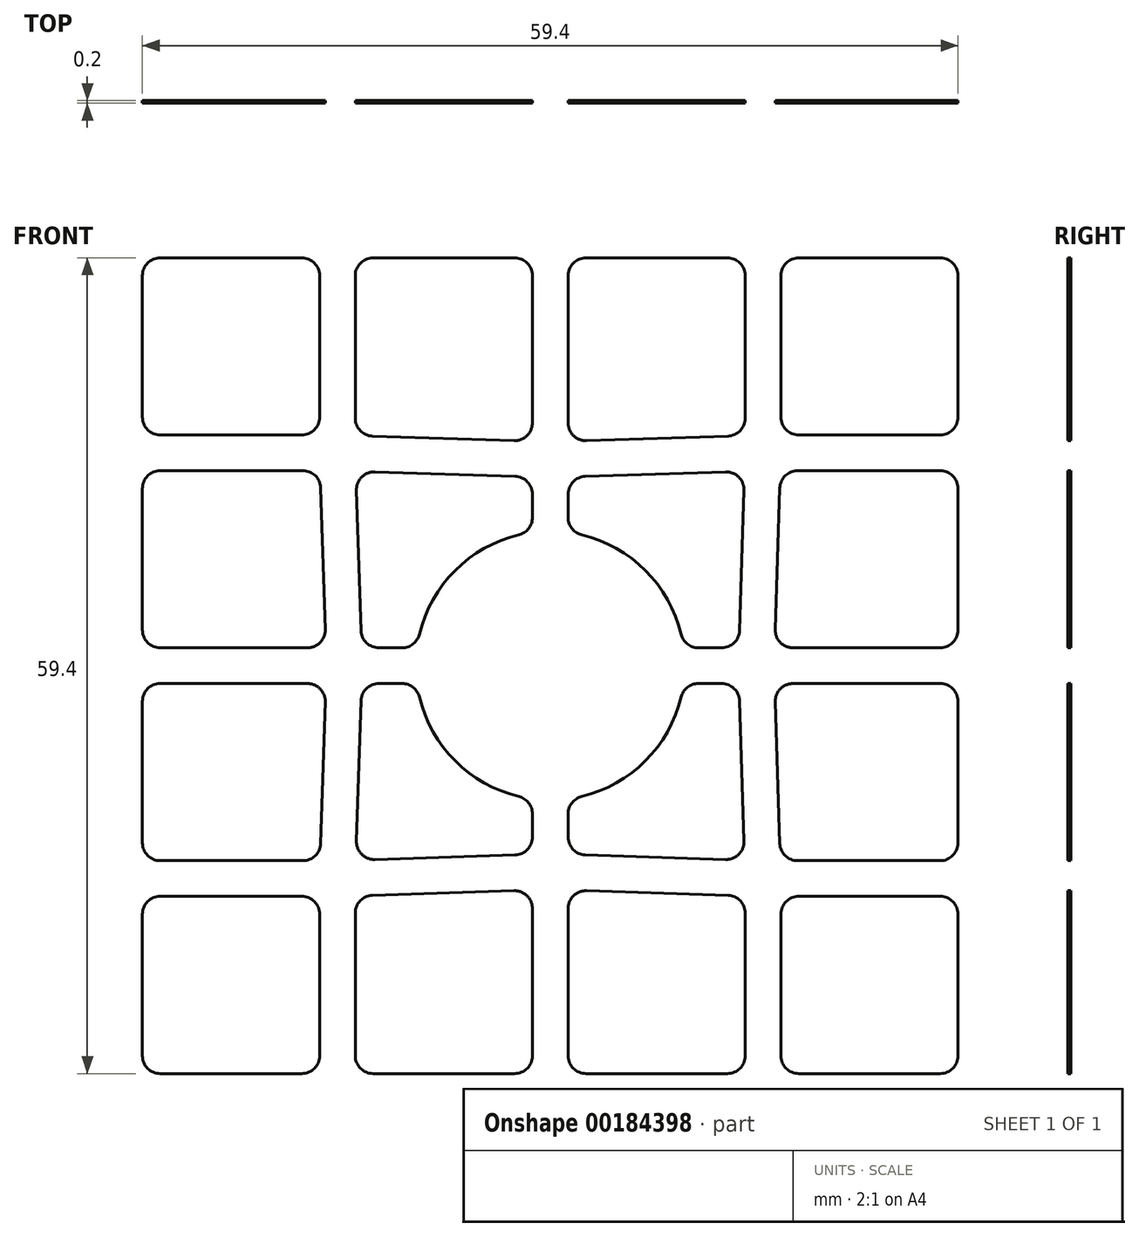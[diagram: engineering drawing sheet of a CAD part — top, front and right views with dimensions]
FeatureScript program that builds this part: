
annotation { "Feature Type Name" : "Feature", "Feature Type Description" : "" }
export const myFeature = defineFeature(function(context is Context, id is Id, definition is map)
    precondition{}
    {
        {
            var Q0;
            Q0=qCreatedBy(makeId("Front.planeOp"),FACE);
            var sketch = newSketch(context, id + "F0", { "sketchPlane" : qUnion([Q0])});
            skLineSegment(sketch, "E0.bottom", {"start": v(0, 0) * mm, "end": v(31, 0) * mm});
            skLineSegment(sketch, "E0.top", {"start": v(0, 31) * mm, "end": v(31, 31) * mm});
            skLineSegment(sketch, "E0.left", {"start": v(0, 0) * mm, "end": v(0, 31) * mm});
            skLineSegment(sketch, "E0.right", {"start": v(31, 0) * mm, "end": v(31, 31) * mm});
            skLineSegment(sketch, "E1", {"start": v(0, 0) * mm, "end": v(31, 31) * mm});
            skLineSegment(sketch, "E2", {"start": v(15.5, 0) * mm, "end": v(15.5, 15.5) * mm});
            skLineSegment(sketch, "E3", {"start": v(15.5, 15.5) * mm, "end": v(31, 16) * mm});
            skLineSegment(sketch, "E4.MirrorCS", {"start": v(15.5, 15.5) * mm, "end": v(16, 31) * mm});
            skLineSegment(sketch, "E5.MirrorCS", {"start": v(0, 15.5) * mm, "end": v(15.5, 15.5) * mm});
            skCircle(sketch, "E6", {"center": v(31, 31) * mm, "radius": 8.5 * mm});
            skSolve(sketch);
        }
        {
            var Q0;
            Q0=qCreatedBy(makeId("Front.planeOp"),FACE);
            var sketch = newSketch(context, id + "F1", { "sketchPlane" : qUnion([Q0])});
            skLineSegment(sketch, "E7.bottom", {"start": v(2.6, 14.2) * mm, "end": v(12.9, 14.2) * mm});
            skLineSegment(sketch, "E7.top", {"start": v(2.6, 1.3) * mm, "end": v(12.9, 1.3) * mm});
            skLineSegment(sketch, "E7.left", {"start": v(1.3, 12.9) * mm, "end": v(1.3, 2.6) * mm});
            skLineSegment(sketch, "E7.right", {"start": v(14.2, 12.9) * mm, "end": v(14.2, 2.6) * mm});
            skLineSegment(sketch, "E8", {"start": v(16.8, 12.98) * mm, "end": v(16.8, 2.6) * mm});
            skLineSegment(sketch, "E9", {"start": v(18.1, 1.3) * mm, "end": v(28.4, 1.3) * mm});
            skLineSegment(sketch, "E10", {"start": v(29.7, 2.6) * mm, "end": v(29.7, 13.31) * mm});
            skLineSegment(sketch, "E11", {"start": v(28.36, 14.61) * mm, "end": v(18.06, 14.28) * mm});
            skLineSegment(sketch, "E12", {"start": v(29.7, 18.52) * mm, "end": v(29.7, 20.2) * mm});
            skLineSegment(sketch, "E13", {"start": v(28.44, 17.22) * mm, "end": v(18.23, 16.89) * mm});
            skLineSegment(sketch, "E14", {"start": v(16.89, 18.23) * mm, "end": v(17.22, 28.44) * mm});
            skLineSegment(sketch, "E15", {"start": v(18.52, 29.7) * mm, "end": v(20.2, 29.7) * mm});
            skLineSegment(sketch, "E16.0", {"start": v(0, 0) * mm, "end": v(31, 31) * mm, "construction": true});
            skArc(sketch, "E17", {"start": v(21.47, 28.7) * mm, "mid": v(24.07, 24.07) * mm, "end": v(28.7, 21.47) * mm});
            skPoint(sketch, "E18.visualSharp", {"position": v(1.3, 14.2) * mm});
            skArc(sketch, "E18.filletArc", {"start": v(2.6, 14.2) * mm, "mid": v(1.68, 13.82) * mm, "end": v(1.3, 12.9) * mm});
            skPoint(sketch, "E19.visualSharp", {"position": v(1.3, 1.3) * mm});
            skArc(sketch, "E19.filletArc", {"start": v(1.3, 2.6) * mm, "mid": v(1.68, 1.68) * mm, "end": v(2.6, 1.3) * mm});
            skPoint(sketch, "E20.visualSharp", {"position": v(14.2, 1.3) * mm});
            skArc(sketch, "E20.filletArc", {"start": v(12.9, 1.3) * mm, "mid": v(13.82, 1.68) * mm, "end": v(14.2, 2.6) * mm});
            skPoint(sketch, "E21.visualSharp", {"position": v(14.2, 14.2) * mm});
            skArc(sketch, "E21.filletArc", {"start": v(14.2, 12.9) * mm, "mid": v(13.82, 13.82) * mm, "end": v(12.9, 14.2) * mm});
            skPoint(sketch, "E22.visualSharp", {"position": v(16.8, 14.24) * mm});
            skArc(sketch, "E22.filletArc", {"start": v(18.06, 14.28) * mm, "mid": v(17.17, 13.89) * mm, "end": v(16.8, 12.98) * mm});
            skPoint(sketch, "E23.visualSharp", {"position": v(16.8, 1.3) * mm});
            skArc(sketch, "E23.filletArc", {"start": v(16.8, 2.6) * mm, "mid": v(17.18, 1.68) * mm, "end": v(18.1, 1.3) * mm});
            skPoint(sketch, "E24.visualSharp", {"position": v(29.7, 14.66) * mm});
            skArc(sketch, "E24.filletArc", {"start": v(29.7, 13.31) * mm, "mid": v(29.3, 14.25) * mm, "end": v(28.36, 14.61) * mm});
            skPoint(sketch, "E25.visualSharp", {"position": v(29.7, 21.29) * mm});
            skArc(sketch, "E25.filletArc", {"start": v(29.7, 20.2) * mm, "mid": v(29.42, 21.01) * mm, "end": v(28.7, 21.47) * mm});
            skPoint(sketch, "E26.visualSharp", {"position": v(17.26, 29.7) * mm});
            skArc(sketch, "E26.filletArc", {"start": v(18.52, 29.7) * mm, "mid": v(17.61, 29.33) * mm, "end": v(17.22, 28.44) * mm});
            skPoint(sketch, "E27.visualSharp", {"position": v(29.7, 1.3) * mm});
            skArc(sketch, "E27.filletArc", {"start": v(28.4, 1.3) * mm, "mid": v(29.32, 1.68) * mm, "end": v(29.7, 2.6) * mm});
            skPoint(sketch, "E28.visualSharp", {"position": v(29.7, 17.26) * mm});
            skArc(sketch, "E28.filletArc", {"start": v(28.44, 17.22) * mm, "mid": v(29.33, 17.61) * mm, "end": v(29.7, 18.52) * mm});
            skPoint(sketch, "E29.visualSharp", {"position": v(21.29, 29.7) * mm});
            skArc(sketch, "E29.filletArc", {"start": v(21.47, 28.7) * mm, "mid": v(21.01, 29.42) * mm, "end": v(20.2, 29.7) * mm});
            skPoint(sketch, "E30.visualSharp", {"position": v(16.84, 16.84) * mm});
            skArc(sketch, "E30.filletArc", {"start": v(16.89, 18.23) * mm, "mid": v(17.27, 17.27) * mm, "end": v(18.23, 16.89) * mm});
            skArc(sketch, "E31.MirrorCS", {"start": v(2.6, 16.8) * mm, "mid": v(1.68, 17.18) * mm, "end": v(1.3, 18.1) * mm});
            skArc(sketch, "E32.MirrorCS", {"start": v(14.28, 18.06) * mm, "mid": v(13.89, 17.17) * mm, "end": v(12.98, 16.8) * mm});
            skArc(sketch, "E33.MirrorCS", {"start": v(13.31, 29.7) * mm, "mid": v(14.25, 29.3) * mm, "end": v(14.61, 28.36) * mm});
            skArc(sketch, "E34.MirrorCS", {"start": v(1.3, 28.4) * mm, "mid": v(1.68, 29.32) * mm, "end": v(2.6, 29.7) * mm});
            skPoint(sketch, "E35.MirrorP", {"position": v(14.66, 29.7) * mm});
            skPoint(sketch, "E36.MirrorP", {"position": v(1.3, 16.8) * mm});
            skPoint(sketch, "E37.MirrorP", {"position": v(1.3, 29.7) * mm});
            skPoint(sketch, "E38.MirrorP", {"position": v(14.24, 16.8) * mm});
            skLineSegment(sketch, "E39.MirrorCS", {"start": v(14.61, 28.36) * mm, "end": v(14.28, 18.06) * mm});
            skLineSegment(sketch, "E40.MirrorCS", {"start": v(12.98, 16.8) * mm, "end": v(2.6, 16.8) * mm});
            skLineSegment(sketch, "E41.MirrorCS", {"start": v(1.3, 18.1) * mm, "end": v(1.3, 28.4) * mm});
            skLineSegment(sketch, "E42.MirrorCS", {"start": v(2.6, 29.7) * mm, "end": v(13.31, 29.7) * mm});
            skArc(sketch, "E43.MirrorCS", {"start": v(45.2, 2.6) * mm, "mid": v(44.82, 1.68) * mm, "end": v(43.9, 1.3) * mm});
            skArc(sketch, "E44.MirrorCS", {"start": v(45.11, 18.23) * mm, "mid": v(44.73, 17.27) * mm, "end": v(43.77, 16.89) * mm});
            skArc(sketch, "E45.MirrorCS", {"start": v(43.94, 14.28) * mm, "mid": v(44.83, 13.89) * mm, "end": v(45.2, 12.98) * mm});
            skArc(sketch, "E46.MirrorCS", {"start": v(43.48, 29.7) * mm, "mid": v(44.39, 29.33) * mm, "end": v(44.78, 28.44) * mm});
            skArc(sketch, "E47.MirrorCS", {"start": v(40.53, 28.7) * mm, "mid": v(40.99, 29.42) * mm, "end": v(41.8, 29.7) * mm});
            skArc(sketch, "E48.MirrorCS", {"start": v(60.7, 28.4) * mm, "mid": v(60.32, 29.32) * mm, "end": v(59.4, 29.7) * mm});
            skArc(sketch, "E49.MirrorCS", {"start": v(32.3, 20.2) * mm, "mid": v(32.58, 21.01) * mm, "end": v(33.3, 21.47) * mm});
            skLineSegment(sketch, "E50.MirrorCS", {"start": v(32.3, 18.52) * mm, "end": v(32.3, 20.2) * mm});
            skArc(sketch, "E51.MirrorCS", {"start": v(33.6, 1.3) * mm, "mid": v(32.68, 1.68) * mm, "end": v(32.3, 2.6) * mm});
            skArc(sketch, "E52.MirrorCS", {"start": v(59.4, 16.8) * mm, "mid": v(60.32, 17.18) * mm, "end": v(60.7, 18.1) * mm});
            skLineSegment(sketch, "E53.MirrorCS", {"start": v(43.48, 29.7) * mm, "end": v(41.8, 29.7) * mm});
            skArc(sketch, "E54.MirrorCS", {"start": v(33.56, 17.22) * mm, "mid": v(32.67, 17.61) * mm, "end": v(32.3, 18.52) * mm});
            skArc(sketch, "E55.MirrorCS", {"start": v(59.4, 14.2) * mm, "mid": v(60.32, 13.82) * mm, "end": v(60.7, 12.9) * mm});
            skArc(sketch, "E56.MirrorCS", {"start": v(48.69, 29.7) * mm, "mid": v(47.75, 29.3) * mm, "end": v(47.39, 28.36) * mm});
            skArc(sketch, "E57.MirrorCS", {"start": v(32.3, 13.31) * mm, "mid": v(32.7, 14.25) * mm, "end": v(33.64, 14.61) * mm});
            skArc(sketch, "E58.MirrorCS", {"start": v(47.72, 18.06) * mm, "mid": v(48.11, 17.17) * mm, "end": v(49.02, 16.8) * mm});
            skArc(sketch, "E59.MirrorCS", {"start": v(60.7, 2.6) * mm, "mid": v(60.32, 1.68) * mm, "end": v(59.4, 1.3) * mm});
            skArc(sketch, "E60.MirrorCS", {"start": v(49.1, 1.3) * mm, "mid": v(48.18, 1.68) * mm, "end": v(47.8, 2.6) * mm});
            skArc(sketch, "E61.MirrorCS", {"start": v(47.8, 12.9) * mm, "mid": v(48.18, 13.82) * mm, "end": v(49.1, 14.2) * mm});
            skPoint(sketch, "E62.MirrorP", {"position": v(32.3, 14.66) * mm});
            skPoint(sketch, "E63.MirrorP", {"position": v(32.3, 1.3) * mm});
            skLineSegment(sketch, "E64.MirrorCS", {"start": v(59.4, 29.7) * mm, "end": v(48.69, 29.7) * mm});
            skPoint(sketch, "E65.MirrorP", {"position": v(60.7, 1.3) * mm});
            skLineSegment(sketch, "E66.MirrorCS", {"start": v(47.39, 28.36) * mm, "end": v(47.72, 18.06) * mm});
            skPoint(sketch, "E67.MirrorP", {"position": v(40.71, 29.7) * mm});
            skPoint(sketch, "E68.MirrorP", {"position": v(45.2, 14.24) * mm});
            skPoint(sketch, "E69.MirrorP", {"position": v(45.16, 16.84) * mm});
            skPoint(sketch, "E70.MirrorP", {"position": v(47.8, 14.2) * mm});
            skLineSegment(sketch, "E71.MirrorCS", {"start": v(33.64, 14.61) * mm, "end": v(43.94, 14.28) * mm});
            skLineSegment(sketch, "E72.MirrorCS", {"start": v(33.56, 17.22) * mm, "end": v(43.77, 16.89) * mm});
            skPoint(sketch, "E73.MirrorP", {"position": v(60.7, 29.7) * mm});
            skPoint(sketch, "E74.MirrorP", {"position": v(60.7, 16.8) * mm});
            skLineSegment(sketch, "E75.MirrorCS", {"start": v(32.3, 2.6) * mm, "end": v(32.3, 13.31) * mm});
            skPoint(sketch, "E76.MirrorP", {"position": v(44.74, 29.7) * mm});
            skLineSegment(sketch, "E77.MirrorCS", {"start": v(45.11, 18.23) * mm, "end": v(44.78, 28.44) * mm});
            skLineSegment(sketch, "E78.MirrorCS", {"start": v(43.9, 1.3) * mm, "end": v(33.6, 1.3) * mm});
            skLineSegment(sketch, "E79.MirrorCS", {"start": v(45.2, 12.98) * mm, "end": v(45.2, 2.6) * mm});
            skPoint(sketch, "E80.MirrorP", {"position": v(47.8, 1.3) * mm});
            skLineSegment(sketch, "E81.MirrorCS", {"start": v(47.8, 12.9) * mm, "end": v(47.8, 2.6) * mm});
            skLineSegment(sketch, "E82.MirrorCS", {"start": v(60.7, 12.9) * mm, "end": v(60.7, 2.6) * mm});
            skArc(sketch, "E83.MirrorCS", {"start": v(40.53, 28.7) * mm, "mid": v(37.93, 24.07) * mm, "end": v(33.3, 21.47) * mm});
            skLineSegment(sketch, "E84.MirrorCS", {"start": v(60.7, 18.1) * mm, "end": v(60.7, 28.4) * mm});
            skLineSegment(sketch, "E85.MirrorCS", {"start": v(59.4, 14.2) * mm, "end": v(49.1, 14.2) * mm});
            skPoint(sketch, "E86.MirrorP", {"position": v(45.2, 1.3) * mm});
            skLineSegment(sketch, "E87.MirrorCS", {"start": v(59.4, 1.3) * mm, "end": v(49.1, 1.3) * mm});
            skLineSegment(sketch, "E88.MirrorCS", {"start": v(49.02, 16.8) * mm, "end": v(59.4, 16.8) * mm});
            skPoint(sketch, "E89.MirrorP", {"position": v(32.3, 21.29) * mm});
            skPoint(sketch, "E90.MirrorP", {"position": v(32.3, 17.26) * mm});
            skPoint(sketch, "E91.MirrorP", {"position": v(60.7, 14.2) * mm});
            skPoint(sketch, "E92.MirrorP", {"position": v(47.76, 16.8) * mm});
            skPoint(sketch, "E93.MirrorP", {"position": v(47.34, 29.7) * mm});
            skArc(sketch, "E94.MirrorCS", {"start": v(16.8, 59.4) * mm, "mid": v(17.18, 60.32) * mm, "end": v(18.1, 60.7) * mm});
            skArc(sketch, "E95.MirrorCS", {"start": v(45.2, 59.4) * mm, "mid": v(44.82, 60.32) * mm, "end": v(43.9, 60.7) * mm});
            skArc(sketch, "E96.MirrorCS", {"start": v(60.7, 59.4) * mm, "mid": v(60.32, 60.32) * mm, "end": v(59.4, 60.7) * mm});
            skLineSegment(sketch, "E97.MirrorCS", {"start": v(32.3, 43.48) * mm, "end": v(32.3, 41.8) * mm});
            skArc(sketch, "E98.MirrorCS", {"start": v(16.89, 43.77) * mm, "mid": v(17.27, 44.73) * mm, "end": v(18.23, 45.11) * mm});
            skArc(sketch, "E99.MirrorCS", {"start": v(18.06, 47.72) * mm, "mid": v(17.17, 48.11) * mm, "end": v(16.8, 49.02) * mm});
            skArc(sketch, "E100.MirrorCS", {"start": v(47.72, 43.94) * mm, "mid": v(48.11, 44.83) * mm, "end": v(49.02, 45.2) * mm});
            skArc(sketch, "E101.MirrorCS", {"start": v(32.3, 41.8) * mm, "mid": v(32.58, 40.99) * mm, "end": v(33.3, 40.53) * mm});
            skArc(sketch, "E102.MirrorCS", {"start": v(21.47, 33.3) * mm, "mid": v(21.01, 32.58) * mm, "end": v(20.2, 32.3) * mm});
            skArc(sketch, "E103.MirrorCS", {"start": v(14.2, 49.1) * mm, "mid": v(13.82, 48.18) * mm, "end": v(12.9, 47.8) * mm});
            skArc(sketch, "E104.MirrorCS", {"start": v(32.3, 48.69) * mm, "mid": v(32.7, 47.75) * mm, "end": v(33.64, 47.39) * mm});
            skLineSegment(sketch, "E105.MirrorCS", {"start": v(18.52, 32.3) * mm, "end": v(20.2, 32.3) * mm});
            skLineSegment(sketch, "E106.MirrorCS", {"start": v(29.7, 43.48) * mm, "end": v(29.7, 41.8) * mm});
            skArc(sketch, "E107.MirrorCS", {"start": v(60.7, 33.6) * mm, "mid": v(60.32, 32.68) * mm, "end": v(59.4, 32.3) * mm});
            skArc(sketch, "E108.MirrorCS", {"start": v(28.44, 44.78) * mm, "mid": v(29.33, 44.39) * mm, "end": v(29.7, 43.48) * mm});
            skArc(sketch, "E109.MirrorCS", {"start": v(1.3, 59.4) * mm, "mid": v(1.68, 60.32) * mm, "end": v(2.6, 60.7) * mm});
            skArc(sketch, "E110.MirrorCS", {"start": v(2.6, 47.8) * mm, "mid": v(1.68, 48.18) * mm, "end": v(1.3, 49.1) * mm});
            skArc(sketch, "E111.MirrorCS", {"start": v(12.9, 60.7) * mm, "mid": v(13.82, 60.32) * mm, "end": v(14.2, 59.4) * mm});
            skArc(sketch, "E112.MirrorCS", {"start": v(48.69, 32.3) * mm, "mid": v(47.75, 32.7) * mm, "end": v(47.39, 33.64) * mm});
            skArc(sketch, "E113.MirrorCS", {"start": v(2.6, 45.2) * mm, "mid": v(1.68, 44.82) * mm, "end": v(1.3, 43.9) * mm});
            skArc(sketch, "E114.MirrorCS", {"start": v(33.6, 60.7) * mm, "mid": v(32.68, 60.32) * mm, "end": v(32.3, 59.4) * mm});
            skArc(sketch, "E115.MirrorCS", {"start": v(40.53, 33.3) * mm, "mid": v(40.99, 32.58) * mm, "end": v(41.8, 32.3) * mm});
            skArc(sketch, "E116.MirrorCS", {"start": v(28.4, 60.7) * mm, "mid": v(29.32, 60.32) * mm, "end": v(29.7, 59.4) * mm});
            skArc(sketch, "E117.MirrorCS", {"start": v(14.28, 43.94) * mm, "mid": v(13.89, 44.83) * mm, "end": v(12.98, 45.2) * mm});
            skArc(sketch, "E118.MirrorCS", {"start": v(29.7, 48.69) * mm, "mid": v(29.3, 47.75) * mm, "end": v(28.36, 47.39) * mm});
            skArc(sketch, "E119.MirrorCS", {"start": v(45.11, 43.77) * mm, "mid": v(44.73, 44.73) * mm, "end": v(43.77, 45.11) * mm});
            skArc(sketch, "E120.MirrorCS", {"start": v(59.4, 45.2) * mm, "mid": v(60.32, 44.82) * mm, "end": v(60.7, 43.9) * mm});
            skArc(sketch, "E121.MirrorCS", {"start": v(47.8, 49.1) * mm, "mid": v(48.18, 48.18) * mm, "end": v(49.1, 47.8) * mm});
            skArc(sketch, "E122.MirrorCS", {"start": v(33.56, 44.78) * mm, "mid": v(32.67, 44.39) * mm, "end": v(32.3, 43.48) * mm});
            skArc(sketch, "E123.MirrorCS", {"start": v(59.4, 47.8) * mm, "mid": v(60.32, 48.18) * mm, "end": v(60.7, 49.1) * mm});
            skArc(sketch, "E124.MirrorCS", {"start": v(43.48, 32.3) * mm, "mid": v(44.39, 32.67) * mm, "end": v(44.78, 33.56) * mm});
            skArc(sketch, "E125.MirrorCS", {"start": v(43.94, 47.72) * mm, "mid": v(44.83, 48.11) * mm, "end": v(45.2, 49.02) * mm});
            skArc(sketch, "E126.MirrorCS", {"start": v(29.7, 41.8) * mm, "mid": v(29.42, 40.99) * mm, "end": v(28.7, 40.53) * mm});
            skArc(sketch, "E127.MirrorCS", {"start": v(1.3, 33.6) * mm, "mid": v(1.68, 32.68) * mm, "end": v(2.6, 32.3) * mm});
            skArc(sketch, "E128.MirrorCS", {"start": v(13.31, 32.3) * mm, "mid": v(14.25, 32.7) * mm, "end": v(14.61, 33.64) * mm});
            skArc(sketch, "E129.MirrorCS", {"start": v(49.1, 60.7) * mm, "mid": v(48.18, 60.32) * mm, "end": v(47.8, 59.4) * mm});
            skLineSegment(sketch, "E130.MirrorCS", {"start": v(43.48, 32.3) * mm, "end": v(41.8, 32.3) * mm});
            skArc(sketch, "E131.MirrorCS", {"start": v(18.52, 32.3) * mm, "mid": v(17.61, 32.67) * mm, "end": v(17.22, 33.56) * mm});
            skPoint(sketch, "E132.MirrorP", {"position": v(1.3, 45.2) * mm});
            skPoint(sketch, "E133.MirrorP", {"position": v(45.2, 60.7) * mm});
            skLineSegment(sketch, "E134.MirrorCS", {"start": v(59.4, 60.7) * mm, "end": v(49.1, 60.7) * mm});
            skLineSegment(sketch, "E135.MirrorCS", {"start": v(32.3, 59.4) * mm, "end": v(32.3, 48.69) * mm});
            skPoint(sketch, "E136.MirrorP", {"position": v(45.16, 45.16) * mm});
            skPoint(sketch, "E137.MirrorP", {"position": v(16.8, 47.76) * mm});
            skPoint(sketch, "E138.MirrorP", {"position": v(16.84, 45.16) * mm});
            skPoint(sketch, "E139.MirrorP", {"position": v(29.7, 40.71) * mm});
            skPoint(sketch, "E140.MirrorP", {"position": v(14.66, 32.3) * mm});
            skLineSegment(sketch, "E141.MirrorCS", {"start": v(59.4, 47.8) * mm, "end": v(49.1, 47.8) * mm});
            skLineSegment(sketch, "E142.MirrorCS", {"start": v(2.6, 32.3) * mm, "end": v(13.31, 32.3) * mm});
            skPoint(sketch, "E143.MirrorP", {"position": v(45.2, 47.76) * mm});
            skLineSegment(sketch, "E144.MirrorCS", {"start": v(33.56, 44.78) * mm, "end": v(43.77, 45.11) * mm});
            skLineSegment(sketch, "E145.MirrorCS", {"start": v(60.7, 43.9) * mm, "end": v(60.7, 33.6) * mm});
            skLineSegment(sketch, "E146.MirrorCS", {"start": v(1.3, 43.9) * mm, "end": v(1.3, 33.6) * mm});
            skLineSegment(sketch, "E147.MirrorCS", {"start": v(16.89, 43.77) * mm, "end": v(17.22, 33.56) * mm});
            skLineSegment(sketch, "E148.MirrorCS", {"start": v(28.44, 44.78) * mm, "end": v(18.23, 45.11) * mm});
            skLineSegment(sketch, "E149.MirrorCS", {"start": v(28.36, 47.39) * mm, "end": v(18.06, 47.72) * mm});
            skPoint(sketch, "E150.MirrorP", {"position": v(40.71, 32.3) * mm});
            skPoint(sketch, "E151.MirrorP", {"position": v(14.2, 47.8) * mm});
            skPoint(sketch, "E152.MirrorP", {"position": v(21.29, 32.3) * mm});
            skLineSegment(sketch, "E153.MirrorCS", {"start": v(29.7, 59.4) * mm, "end": v(29.7, 48.69) * mm});
            skLineSegment(sketch, "E154.MirrorCS", {"start": v(33.64, 47.39) * mm, "end": v(43.94, 47.72) * mm});
            skLineSegment(sketch, "E155.MirrorCS", {"start": v(18.1, 60.7) * mm, "end": v(28.4, 60.7) * mm});
            skLineSegment(sketch, "E156.MirrorCS", {"start": v(16.8, 49.02) * mm, "end": v(16.8, 59.4) * mm});
            skLineSegment(sketch, "E157.MirrorCS", {"start": v(14.2, 49.1) * mm, "end": v(14.2, 59.4) * mm});
            skLineSegment(sketch, "E158.MirrorCS", {"start": v(1.3, 49.1) * mm, "end": v(1.3, 59.4) * mm});
            skLineSegment(sketch, "E159.MirrorCS", {"start": v(2.6, 60.7) * mm, "end": v(12.9, 60.7) * mm});
            skLineSegment(sketch, "E160.MirrorCS", {"start": v(2.6, 47.8) * mm, "end": v(12.9, 47.8) * mm});
            skPoint(sketch, "E161.MirrorP", {"position": v(47.8, 60.7) * mm});
            skArc(sketch, "E162.MirrorCS", {"start": v(21.47, 33.3) * mm, "mid": v(24.07, 37.93) * mm, "end": v(28.7, 40.53) * mm});
            skLineSegment(sketch, "E163.MirrorCS", {"start": v(12.98, 45.2) * mm, "end": v(2.6, 45.2) * mm});
            skPoint(sketch, "E164.MirrorP", {"position": v(60.7, 60.7) * mm});
            skPoint(sketch, "E165.MirrorP", {"position": v(29.7, 60.7) * mm});
            skPoint(sketch, "E166.MirrorP", {"position": v(1.3, 60.7) * mm});
            skPoint(sketch, "E167.MirrorP", {"position": v(60.7, 47.8) * mm});
            skPoint(sketch, "E168.MirrorP", {"position": v(47.8, 47.8) * mm});
            skLineSegment(sketch, "E169.MirrorCS", {"start": v(45.11, 43.77) * mm, "end": v(44.78, 33.56) * mm});
            skPoint(sketch, "E170.MirrorP", {"position": v(29.7, 44.74) * mm});
            skLineSegment(sketch, "E171.MirrorCS", {"start": v(47.39, 33.64) * mm, "end": v(47.72, 43.94) * mm});
            skPoint(sketch, "E172.MirrorP", {"position": v(47.34, 32.3) * mm});
            skPoint(sketch, "E173.MirrorP", {"position": v(32.3, 60.7) * mm});
            skPoint(sketch, "E174.MirrorP", {"position": v(1.3, 32.3) * mm});
            skPoint(sketch, "E175.MirrorP", {"position": v(17.26, 32.3) * mm});
            skPoint(sketch, "E176.MirrorP", {"position": v(60.7, 45.2) * mm});
            skPoint(sketch, "E177.MirrorP", {"position": v(14.2, 60.7) * mm});
            skPoint(sketch, "E178.MirrorP", {"position": v(32.3, 40.71) * mm});
            skPoint(sketch, "E179.MirrorP", {"position": v(14.24, 45.2) * mm});
            skPoint(sketch, "E180.MirrorP", {"position": v(32.3, 44.74) * mm});
            skPoint(sketch, "E181.MirrorP", {"position": v(29.7, 47.34) * mm});
            skLineSegment(sketch, "E182.MirrorCS", {"start": v(49.02, 45.2) * mm, "end": v(59.4, 45.2) * mm});
            skLineSegment(sketch, "E183.MirrorCS", {"start": v(45.2, 49.02) * mm, "end": v(45.2, 59.4) * mm});
            skLineSegment(sketch, "E184.MirrorCS", {"start": v(47.8, 49.1) * mm, "end": v(47.8, 59.4) * mm});
            skPoint(sketch, "E185.MirrorP", {"position": v(16.8, 60.7) * mm});
            skPoint(sketch, "E186.MirrorP", {"position": v(44.74, 32.3) * mm});
            skArc(sketch, "E187.MirrorCS", {"start": v(40.53, 33.3) * mm, "mid": v(37.93, 37.93) * mm, "end": v(33.3, 40.53) * mm});
            skLineSegment(sketch, "E188.MirrorCS", {"start": v(43.9, 60.7) * mm, "end": v(33.6, 60.7) * mm});
            skPoint(sketch, "E189.MirrorP", {"position": v(60.7, 32.3) * mm});
            skPoint(sketch, "E190.MirrorP", {"position": v(1.3, 47.8) * mm});
            skPoint(sketch, "E191.MirrorP", {"position": v(47.76, 45.2) * mm});
            skPoint(sketch, "E192.MirrorP", {"position": v(32.3, 47.34) * mm});
            skLineSegment(sketch, "E193.MirrorCS", {"start": v(59.4, 32.3) * mm, "end": v(48.69, 32.3) * mm});
            skLineSegment(sketch, "E194.MirrorCS", {"start": v(14.61, 33.64) * mm, "end": v(14.28, 43.94) * mm});
            skLineSegment(sketch, "E195.MirrorCS", {"start": v(60.7, 49.1) * mm, "end": v(60.7, 59.4) * mm});
            skSolve(sketch);
        }
        {
            var Q0;
            Q0 = qSketchRegion(id + "F1", true);
            extrude(context, id + "F2", {"entities" : qUnion([Q0]), "depth" : 0.2 * mm});
        }
    });
